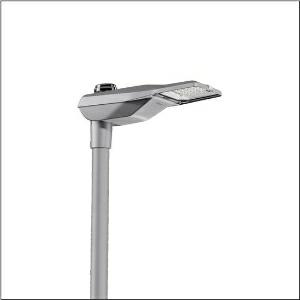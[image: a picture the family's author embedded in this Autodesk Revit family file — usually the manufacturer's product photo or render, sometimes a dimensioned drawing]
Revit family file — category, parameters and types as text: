
# Revit family: streetlight_sl_21_micro___stw1_0a_5xe5e37n08db_8c5c
name_source: partatom
category: Lighting Fixtures
units: mm (PartAtom-declared; Revit-internal decimal feet)

## family parameters
Cut with Voids When Loaded = No
Host = Face
Light Source = No
Part Type = Normal
Room Calculation Point = No
Round Connector Dimension = Use Diameter
Shared = No

## types (1)
- --- (1 x LED, 5110 lm, 39.1 W, 3000K)
    Apparent Load = 39 VA
    CIE Flux Codes = 38 75 98 100 100
    Color Rendering = 70
    Color Temperature = 3000K
    Default Elevation = 1800 mm
    Description = Streetlight SL 21 micro, mast luminaire, primary light control with lens, of PMMA, primary optical cover: cover, of toughened safety glass, transparent, light distribution: STW1.0a, light emission: direct distribution, primary light characteristic: asymmetric, installation type: post-top, LED, 3G 1.5mm², High Power LED, rated luminous flux: 5.110lm, luminous efficacy: 131lm/W, light colour: 730, colour temperature: 3000K, control gear: NEMA (7pin), control: overheat protection, pre-setting: linear dimming characteristic, constant luminous flux control, time-dependent luminous flux control, flexible luminous flux parameterisation, mains connection: 230..240V, AC, 50/60Hz, connection cable pre-assembled, cable length: 6,5m, wiring characteristics: H07RN-F, start of lifetime: 39W, end of service life: 41W, reduction: 18W, luminaire housing, of diecast aluminium (EN AC-44300), powder-coated, SITECO metallic grey (DB 702S), corrosivity category C5 high according to DIN EN ISO 12944, multi-level sealing system, sealing non-destructively replaceable, inclination adjustable: 0°, 5°, 10°, 15°, length: 528mm, width: 235mm, height: 110mm, spigot size: 76/60mm (post-top), mounting height: 4..8m, protection rating (complete): IP66, insulation class (complete): insulation class I (protective earthing), certification: CE, ENEC, ENEC+, VDE, impact resistance: IK10, permissible operating ambient temperature for outdoor applications: -40..+50°C, standard-compliant lighting for roads and squares, packaging unit: 1 piece

Light Distribution: STW1.0a
    Height = 110 mm
    Lamp = 1 x LED
    Lamp Light Flux = 5110 lm
    Lamp Power = 39.1 W
    Lamp count = 1
    Length = 528 mm
    Luminous efficacy = 131 lm/W
    Manufacturer = Siteco
    ModVariant = No
    Model = 5XE5E37N08DB
    Number of Poles = 1
    OnlyDefault = Yes
    Power Factor = 1
    Product Name = Streetlight SL 21 micro | STW1.0a
    Product group = mast luminaire | pylon top
    ProductGroupID = 6100
    Protection Class = Protection class I
    Protection Degree = IP 66
    RLX_Detail_Level = 1
    RLX_Emergency_Light_Flux = 0 lm
    RLX_Emergency_Type = 0
    RLX_Emergency_Type_DB = No
    RlxData = <blob elided: 99289 chars, md5=3b1455ea>
    Socket = socket
    Standby Power = 0 W
    System Light Flux = 5110 lm
    System Power = 39 W
    Type Comments = factory setting: luminous flux: 100 % | dim-lin: 254 | 765 mA
    Type Image = l_1294375.jpg
    URL = http://relux.com
    VarID = @adj_135319
    Voltage = 0 V
    Weight = 0.00 kg
    Width = 235 mm

## geometry (parser evidence)
native form markers: Blend x4, Sweep x10
no freeform markers — native parametric forms only
